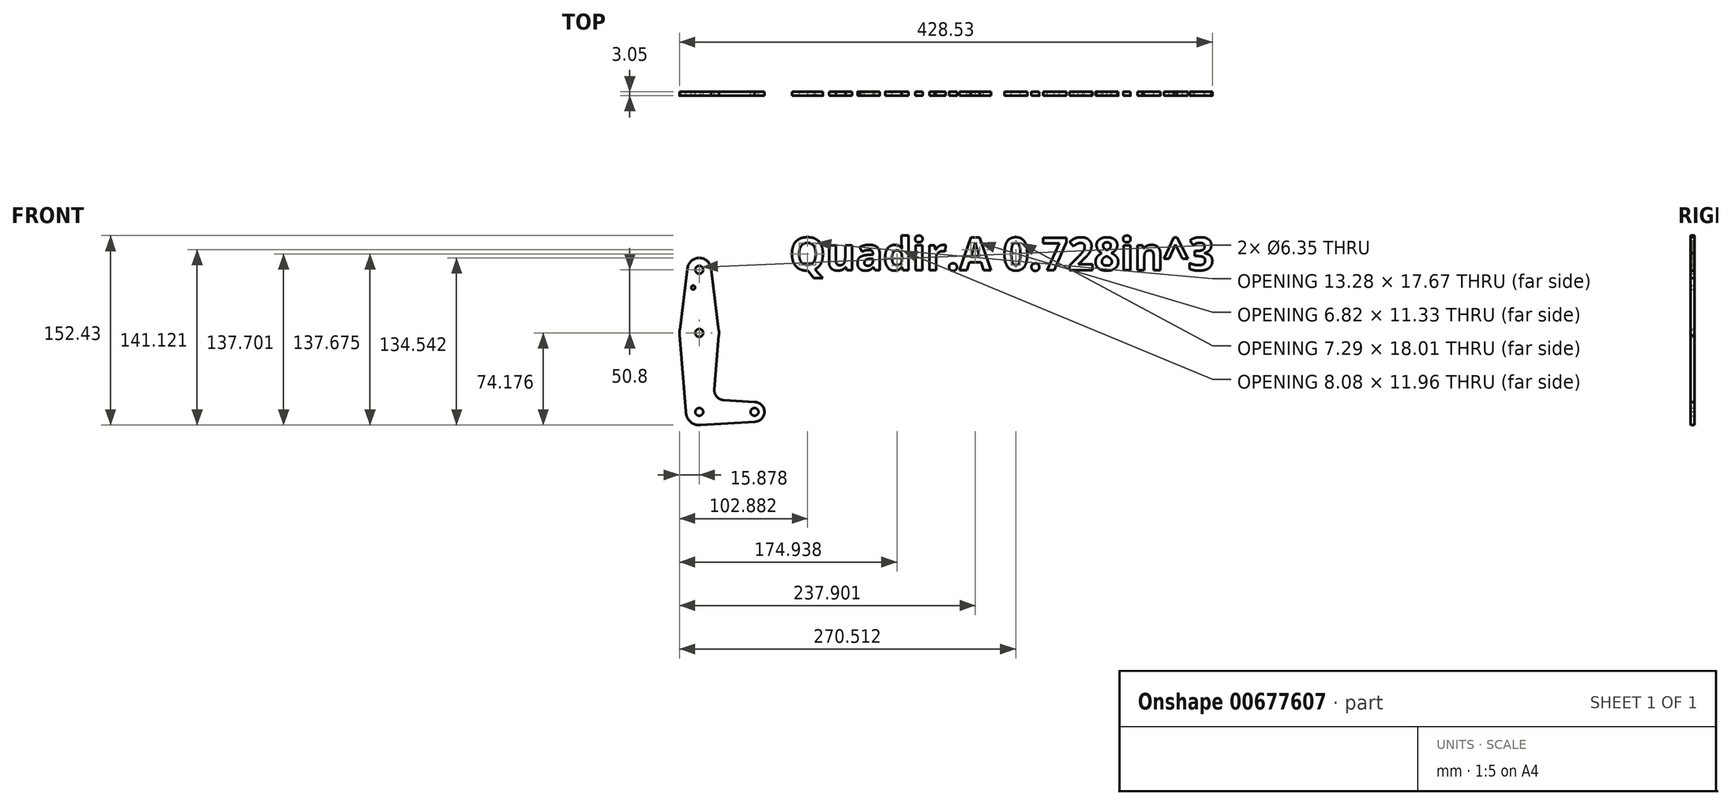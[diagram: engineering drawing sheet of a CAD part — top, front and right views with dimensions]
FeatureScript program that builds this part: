
annotation { "Feature Type Name" : "Feature", "Feature Type Description" : "" }
export const myFeature = defineFeature(function(context is Context, id is Id, definition is map)
    precondition{}
    {
        {
            var Q0;
            Q0=qCreatedBy(makeId("Front.planeOp"),FACE);
            var sketch = newSketch(context, id + "F0", { "sketchPlane" : qUnion([Q0])});
            skLineSegment(sketch, "E0", {"start": v(-29.86, 77.28) * mm, "end": v(-29.86, -37.02) * mm, "construction": true});
            skLineSegment(sketch, "E1", {"start": v(-29.86, -37.02) * mm, "end": v(14.59, -37.02) * mm, "construction": true});
            skCircle(sketch, "E2", {"center": v(-29.86, 77.28) * mm, "radius": 9.53 * mm});
            skCircle(sketch, "E3", {"center": v(-29.86, 26.48) * mm, "radius": 15.88 * mm});
            skCircle(sketch, "E4", {"center": v(-29.86, -37.02) * mm, "radius": 10.67 * mm});
            skCircle(sketch, "E5", {"center": v(14.59, -37.02) * mm, "radius": 7.94 * mm});
            skLineSegment(sketch, "E6", {"start": v(-20.35, 77.79) * mm, "end": v(-14.11, 28.47) * mm});
            skLineSegment(sketch, "E7", {"start": v(-14.11, 28.47) * mm, "end": v(-14.11, 24.48) * mm});
            skLineSegment(sketch, "E8", {"start": v(-14.11, 24.48) * mm, "end": v(-17.7, -18.97) * mm});
            skLineSegment(sketch, "E9", {"start": v(-40.53, -36.87) * mm, "end": v(-45.68, 25.16) * mm});
            skLineSegment(sketch, "E10", {"start": v(-45.68, 27.79) * mm, "end": v(-39.31, 78.46) * mm});
            skLineSegment(sketch, "E11", {"start": v(-10.26, -27.56) * mm, "end": v(14.59, -29.09) * mm});
            skLineSegment(sketch, "E12", {"start": v(-29.7, -47.7) * mm, "end": v(15.07, -44.95) * mm});
            skCircle(sketch, "E13", {"center": v(-29.86, 77.28) * mm, "radius": 3.18 * mm});
            skCircle(sketch, "E14", {"center": v(-34.74, 63) * mm, "radius": 1.59 * mm});
            skCircle(sketch, "E15", {"center": v(-29.86, 26.48) * mm, "radius": 3.18 * mm});
            skCircle(sketch, "E16", {"center": v(-29.86, -37.02) * mm, "radius": 3.13 * mm});
            skCircle(sketch, "E17", {"center": v(14.59, -37.02) * mm, "radius": 3.13 * mm});
            skArc(sketch, "E18.filletArc", {"start": v(-17.7, -18.97) * mm, "mid": v(-15.79, -24.83) * mm, "end": v(-10.26, -27.56) * mm});
            skText(sketch, "E19", { "text": "Quadir.A 0.728in^3", "fontName": "OpenSans-Bold.ttf"});
            const initialGuessF0  = {"E19": [0.04255, 0.07687, 1, 0, 0.0264]};
            skSetInitialGuess(sketch, initialGuessF0);
            skSolve(sketch);
        }
        {
            var Q0;
            Q0 = qSketchRegion(id + "F0", true);
            var Q1;
            Q1=sQuery(id+"F0.wireOp",EDGE,"E6");
            var Q2;
            Q2=sQuery(id+"F0.wireOp",EDGE,"E10");
            var Q3;
            Q3=sQuery(id+"F0.wireOp",EDGE,"E12");
            var Q4;
            Q4=sQuery(id+"F0.wireOp",EDGE,"E9");
            var Q5;
            Q5=sQuery(id+"F0.wireOp",EDGE,"E11");
            var Q6;
            Q6=sQuery(id+"F0.wireOp",EDGE,"E18.filletArc");
            var Q7;
            Q7=sQuery(id+"F0.wireOp",EDGE,"E8");
            var Q8;
            Q8=sQuery(id+"F0.wireOp",EDGE,"E4");
            var Q9;
            Q9=sQuery(id+"F0.wireOp",EDGE,"E5");
            var Q10;
            Q10=sQuery(id+"F0.wireOp",EDGE,"E3");
            var Q11;
            Q11=sQuery(id+"F0.wireOp",EDGE,"E2");
            var Q12;
            Q12=sQuery(id+"F0.wireOp",EDGE,"E13");
            var Q13;
            Q13=sQuery(id+"F0.wireOp",EDGE,"E14");
            var Q14;
            Q14=sQuery(id+"F0.wireOp",EDGE,"E15");
            var Q15;
            Q15=sQuery(id+"F0.wireOp",EDGE,"E16");
            var Q16;
            Q16=sQuery(id+"F0.wireOp",EDGE,"E17");
            extrude(context, id + "F1", {"entities" : qUnion([Q0]), "surfaceEntities" : qUnion([Q1, Q2, Q3, Q4, Q5, Q6, Q7, Q8, Q9, Q10, Q11, Q12, Q13, Q14, Q15, Q16]), "depth" : 3.05 * mm, "offsetDistance" : 25.4 * mm});
        }
    });
